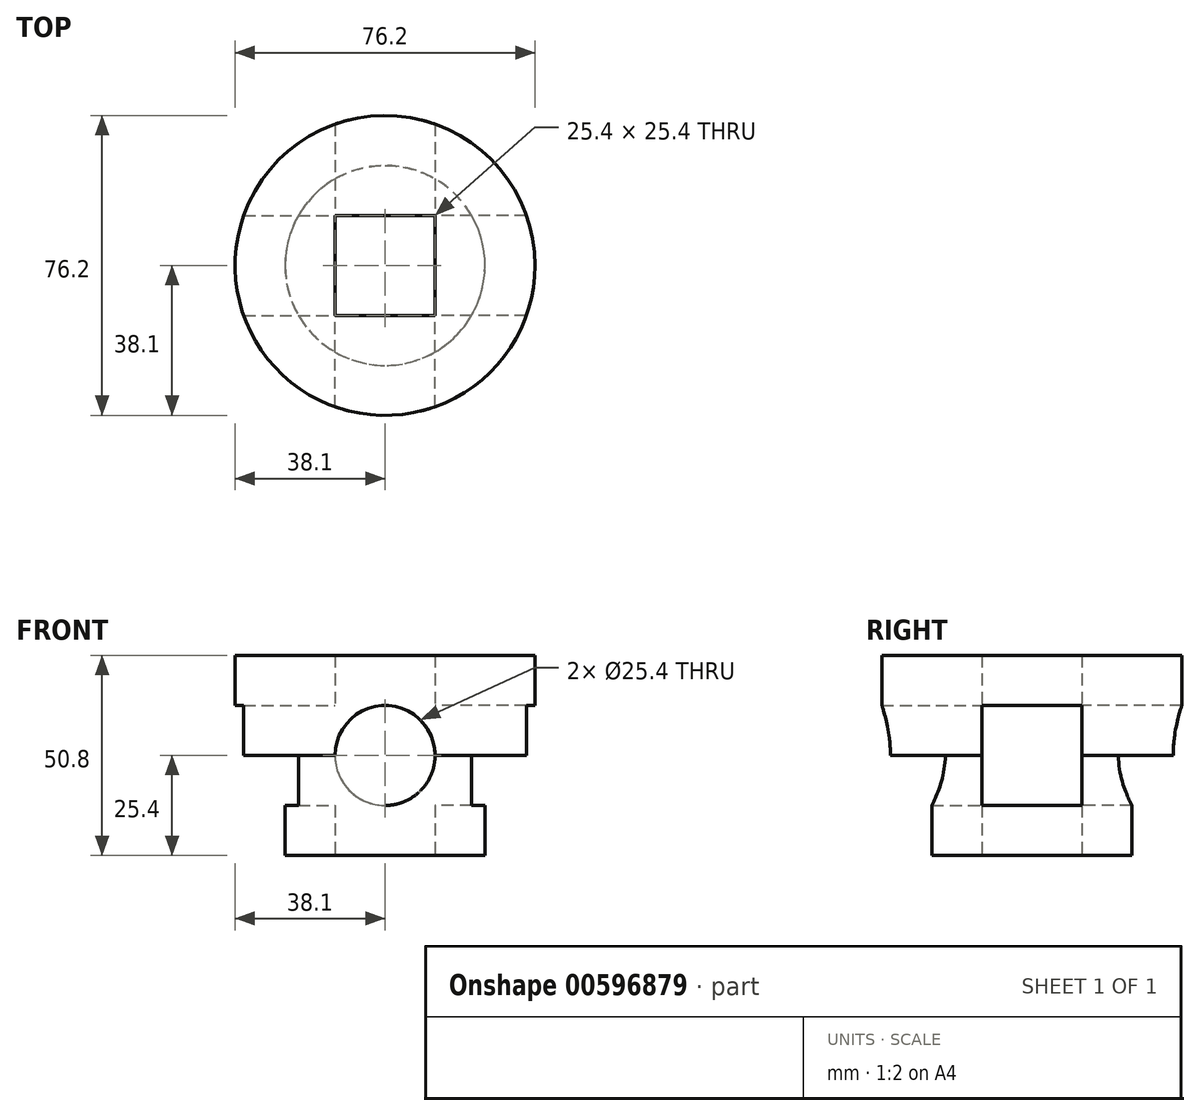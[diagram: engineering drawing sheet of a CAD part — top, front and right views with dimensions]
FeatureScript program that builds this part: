
annotation { "Feature Type Name" : "Feature", "Feature Type Description" : "" }
export const myFeature = defineFeature(function(context is Context, id is Id, definition is map)
    precondition{}
    {
        {
            var Q0;
            Q0=qCreatedBy(makeId("Top.planeOp"),FACE);
            var sketch = newSketch(context, id + "F0", { "sketchPlane" : qUnion([Q0])});
            skPoint(sketch, "E0.middle", {"position": v(0, 0) * mm});
            skCircle(sketch, "E1", {"center": v(0, 0) * mm, "radius": 38.1 * mm});
            skSolve(sketch);
        }
        {
            var Q0;
            Q0=makeQuery(id+"F0.imprint","IMPRINT",FACE,{"disambiguationData":[TD([[makeQuery(id+"F0.imprint","IMPRINT",EDGE,{"derivedFrom":sQuery(id+"F0.wireOp",EDGE,"E1")}),1.0]])]});
            extrude(context, id + "F1", {"entities" : qUnion([Q0]), "depth" : 25.4 * mm, "offsetDistance" : 25.4 * mm});
        }
        {
            var Q0;
            Q0=makeQuery(id+"F1.opExtrude","CAP_FACE",FACE,{"disambiguationData":[OSD([sQuery(id+"F0.wireOp",EDGE,"E1")])],"isStart":false});
            var sketch = newSketch(context, id + "F2", { "sketchPlane" : qUnion([Q0])});
            skLineSegment(sketch, "E2.bottom", {"start": v(12.7, -12.7) * mm, "end": v(-12.7, -12.7) * mm});
            skLineSegment(sketch, "E2.top", {"start": v(12.7, 12.7) * mm, "end": v(-12.7, 12.7) * mm});
            skLineSegment(sketch, "E2.left", {"start": v(12.7, -12.7) * mm, "end": v(12.7, 12.7) * mm});
            skLineSegment(sketch, "E2.right", {"start": v(-12.7, -12.7) * mm, "end": v(-12.7, 12.7) * mm});
            skPoint(sketch, "E2.middle", {"position": v(0, 0) * mm});
            skSolve(sketch);
        }
        {
            var Q0;
            Q0 = qSketchRegion(id + "F2", true);
            extrude(context, id + "F3", {"entities" : qUnion([Q0]), "operationType" : NewBodyOperationType.ADD, "depth" : 25.4 * mm, "offsetDistance" : 25.4 * mm});
        }
        {
            var Q0;
            Q0=makeQuery(id+"F1.opExtrude","CAP_FACE",FACE,{"disambiguationData":[OSD([sQuery(id+"F0.wireOp",EDGE,"E1")])],"isStart":true});
            var sketch = newSketch(context, id + "F4", { "sketchPlane" : qUnion([Q0])});
            skCircle(sketch, "E3", {"center": v(0, 0) * mm, "radius": 25.4 * mm});
            skSolve(sketch);
        }
        {
            var Q0;
            Q0=makeQuery(id+"F4.imprint","IMPRINT",FACE,{"disambiguationData":[TD([[makeQuery(id+"F4.imprint","IMPRINT",EDGE,{"derivedFrom":sQuery(id+"F4.wireOp",EDGE,"E3")}),1.0]])]});
            extrude(context, id + "F5", {"entities" : qUnion([Q0]), "operationType" : NewBodyOperationType.ADD, "depth" : 25.4 * mm, "offsetDistance" : 25.4 * mm});
        }
        {
            var Q0;
            Q0=makeQuery(id+"F5.opExtrude","CAP_FACE",FACE,{"disambiguationData":[OSD([sQuery(id+"F4.wireOp",EDGE,"E3")])],"isStart":false});
            var sketch = newSketch(context, id + "F6", { "sketchPlane" : qUnion([Q0])});
            skLineSegment(sketch, "E4.bottom", {"start": v(12.7, 12.7) * mm, "end": v(-12.7, 12.7) * mm});
            skLineSegment(sketch, "E4.top", {"start": v(12.7, -12.7) * mm, "end": v(-12.7, -12.7) * mm});
            skLineSegment(sketch, "E4.left", {"start": v(12.7, 12.7) * mm, "end": v(12.7, -12.7) * mm});
            skLineSegment(sketch, "E4.right", {"start": v(-12.7, 12.7) * mm, "end": v(-12.7, -12.7) * mm});
            skPoint(sketch, "E4.middle", {"position": v(0, 0) * mm});
            skSolve(sketch);
        }
        {
            var Q0;
            Q0 = qSketchRegion(id + "F6", true);
            extrude(context, id + "F7", {"entities" : qUnion([Q0]), "operationType" : NewBodyOperationType.REMOVE, "endBound" : BoundingType.THROUGH_ALL, "depth" : 25.4 * mm, "offsetDistance" : 25.4 * mm});
        }
        {
            var Q0;
            Q0=makeQuery(id+"F5.opExtrude","CAP_FACE",FACE,{"disambiguationData":[OSD([sQuery(id+"F4.wireOp",EDGE,"E3")])],"isStart":false});
            var sketch = newSketch(context, id + "F8", { "sketchPlane" : qUnion([Q0])});
            skLineSegment(sketch, "E5.bottom", {"start": v(12.7, 12.7) * mm, "end": v(-12.7, 12.7) * mm});
            skLineSegment(sketch, "E5.top", {"start": v(12.7, -12.7) * mm, "end": v(-12.7, -12.7) * mm});
            skLineSegment(sketch, "E5.left", {"start": v(12.7, 12.7) * mm, "end": v(12.7, -12.7) * mm});
            skLineSegment(sketch, "E5.right", {"start": v(-12.7, 12.7) * mm, "end": v(-12.7, -12.7) * mm});
            skPoint(sketch, "E5.middle", {"position": v(0, 0) * mm});
            skSolve(sketch);
        }
        {
            var Q0;
            Q0 = qSketchRegion(id + "F8", true);
            extrude(context, id + "F9", {"entities" : qUnion([Q0]), "operationType" : NewBodyOperationType.REMOVE, "endBound" : BoundingType.THROUGH_ALL, "oppositeDirection" : true, "depth" : 25.4 * mm, "offsetDistance" : 25.4 * mm});
        }
        {
            var Q0;
            Q0=qCreatedBy(makeId("Front.planeOp"),FACE);
            var sketch = newSketch(context, id + "F10", { "sketchPlane" : qUnion([Q0])});
            skCircle(sketch, "E6", {"center": v(0, 0) * mm, "radius": 12.7 * mm});
            skSolve(sketch);
        }
        {
            var Q0;
            Q0 = qSketchRegion(id + "F10", true);
            extrude(context, id + "F11", {"entities" : qUnion([Q0]), "operationType" : NewBodyOperationType.REMOVE, "endBound" : BoundingType.THROUGH_ALL, "oppositeDirection" : true, "depth" : 25.4 * mm, "offsetDistance" : 25.4 * mm});
        }
        {
            var Q0;
            Q0=makeQuery(id+"F10.imprint","IMPRINT",FACE,{"disambiguationData":[TD([[makeQuery(id+"F10.imprint","IMPRINT",EDGE,{"derivedFrom":sQuery(id+"F10.wireOp",EDGE,"E6")}),1.0]])]});
            extrude(context, id + "F12", {"entities" : qUnion([Q0]), "operationType" : NewBodyOperationType.REMOVE, "depth" : 50.8 * mm, "offsetDistance" : 25.4 * mm});
        }
        {
            var Q0;
            Q0=qCreatedBy(makeId("Right.planeOp"),FACE);
            var sketch = newSketch(context, id + "F13", { "sketchPlane" : qUnion([Q0])});
            skLineSegment(sketch, "E7.bottom", {"start": v(12.7, 12.7) * mm, "end": v(-12.7, 12.7) * mm});
            skLineSegment(sketch, "E7.top", {"start": v(12.7, -12.7) * mm, "end": v(-12.7, -12.7) * mm});
            skLineSegment(sketch, "E7.left", {"start": v(12.7, 12.7) * mm, "end": v(12.7, -12.7) * mm});
            skLineSegment(sketch, "E7.right", {"start": v(-12.7, 12.7) * mm, "end": v(-12.7, -12.7) * mm});
            skPoint(sketch, "E7.middle", {"position": v(0, 0) * mm});
            skSolve(sketch);
        }
        {
            var Q0;
            Q0 = qSketchRegion(id + "F13", true);
            extrude(context, id + "F14", {"entities" : qUnion([Q0]), "operationType" : NewBodyOperationType.REMOVE, "endBound" : BoundingType.THROUGH_ALL, "oppositeDirection" : true, "depth" : 25.4 * mm, "offsetDistance" : 25.4 * mm});
        }
        {
            var Q0;
            Q0=makeQuery(id+"F14.boolean.opBoolean","SPLIT",FACE,{"disambiguationData":[TD([makeQuery(id+"F5.opExtrude","CAP_FACE",FACE,{"disambiguationData":[OSD([sQuery(id+"F4.wireOp",EDGE,"E3")])],"isStart":false})])],"derivedFrom":makeQuery(id+"F9.boolean.opBoolean","COPY",FACE,{"derivedFrom":makeQuery(id+"F9.opExtrude","SWEPT_FACE",FACE,{"disambiguationData":[OSD([sQuery(id+"F8.wireOp",EDGE,"E5.right")])]})})});
            var sketch = newSketch(context, id + "F15", { "sketchPlane" : qUnion([Q0])});
            skLineSegment(sketch, "E8.bottom", {"start": v(12.7, 12.7) * mm, "end": v(-12.7, 12.7) * mm});
            skLineSegment(sketch, "E8.top", {"start": v(12.7, -12.7) * mm, "end": v(-12.7, -12.7) * mm});
            skLineSegment(sketch, "E8.left", {"start": v(12.7, 12.7) * mm, "end": v(12.7, -12.7) * mm});
            skLineSegment(sketch, "E8.right", {"start": v(-12.7, 12.7) * mm, "end": v(-12.7, -12.7) * mm});
            skPoint(sketch, "E8.middle", {"position": v(0, 0) * mm});
            skSolve(sketch);
        }
        {
            var Q0;
            Q0 = qSketchRegion(id + "F15", true);
            extrude(context, id + "F16", {"entities" : qUnion([Q0]), "operationType" : NewBodyOperationType.REMOVE, "endBound" : BoundingType.THROUGH_ALL, "depth" : 25.4 * mm, "offsetDistance" : 25.4 * mm});
        }
    });
